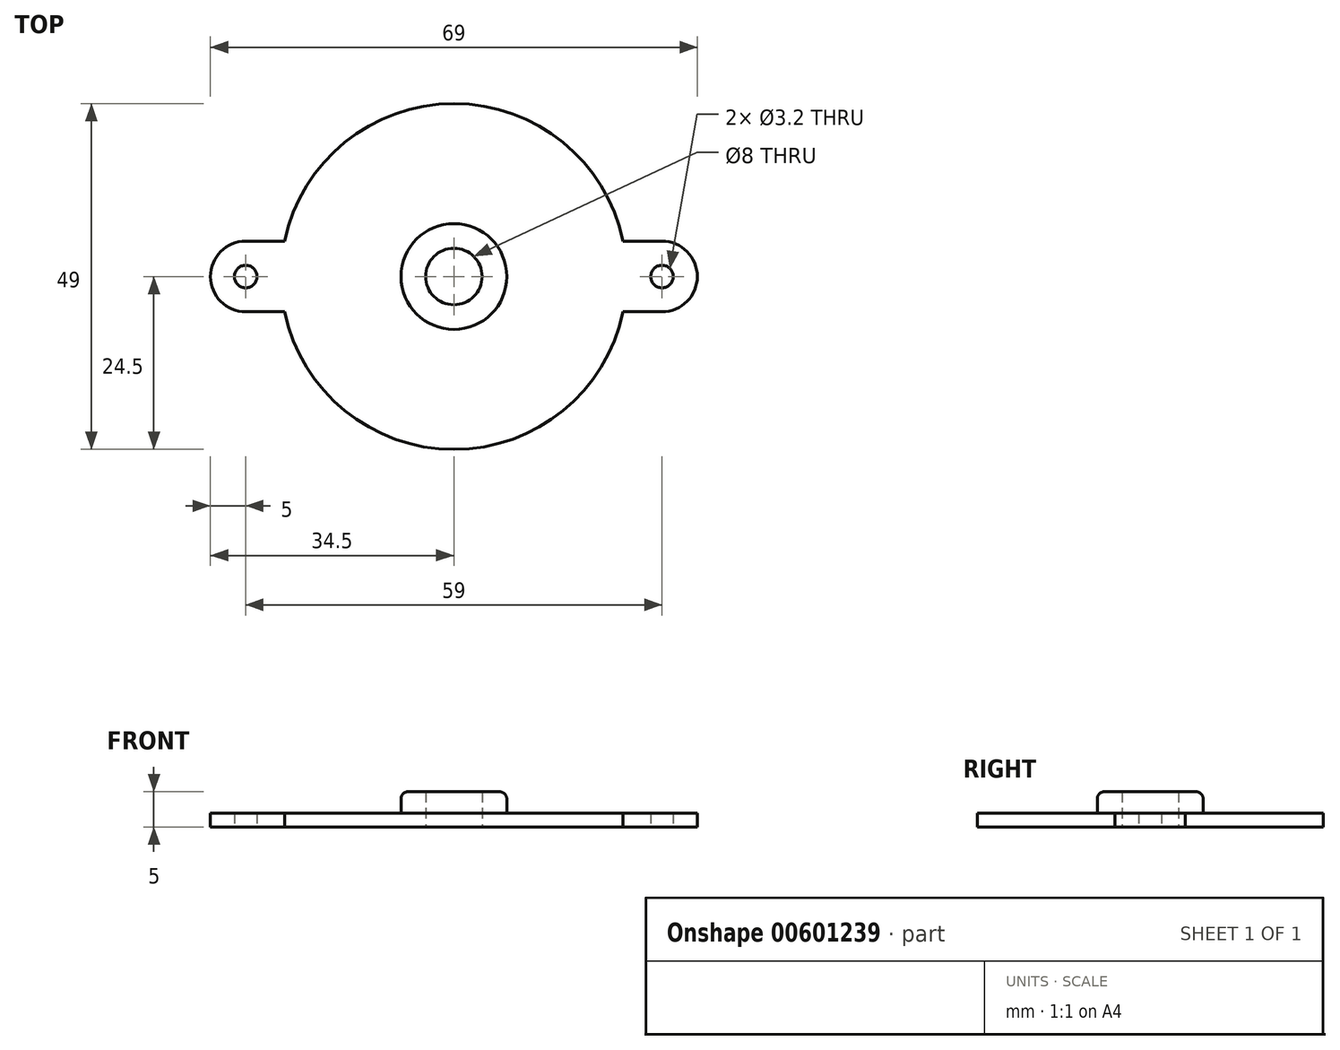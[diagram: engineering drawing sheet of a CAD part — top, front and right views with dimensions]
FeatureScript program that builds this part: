
annotation { "Feature Type Name" : "Feature", "Feature Type Description" : "" }
export const myFeature = defineFeature(function(context is Context, id is Id, definition is map)
    precondition{}
    {
        {
            var Q0;
            Q0=qCreatedBy(makeId("Top.planeOp"),FACE);
            var sketch = newSketch(context, id + "F0", { "sketchPlane" : qUnion([Q0])});
            skCircle(sketch, "E0", {"center": v(-29.5, 0) * mm, "radius": 5 * mm});
            skCircle(sketch, "E1", {"center": v(29.5, 0) * mm, "radius": 5 * mm});
            skCircle(sketch, "E2", {"center": v(-29.5, 0) * mm, "radius": 1.6 * mm});
            skCircle(sketch, "E3", {"center": v(29.5, 0) * mm, "radius": 1.6 * mm});
            skCircle(sketch, "E4", {"center": v(0, 0) * mm, "radius": 24.5 * mm});
            skLineSegment(sketch, "E5", {"start": v(-29.5, 5) * mm, "end": v(-23.98, 5) * mm});
            skLineSegment(sketch, "E6", {"start": v(-29.5, -5) * mm, "end": v(-23.98, -5) * mm});
            skLineSegment(sketch, "E7", {"start": v(23.98, -5) * mm, "end": v(29.5, -5) * mm});
            skLineSegment(sketch, "E8", {"start": v(23.98, 5) * mm, "end": v(29.5, 5) * mm});
            skCircle(sketch, "E9", {"center": v(0, 0) * mm, "radius": 4 * mm});
            skSolve(sketch);
        }
        {
            var Q0;
            Q0=makeQuery(id+"F0.imprint","IMPRINT",FACE,{"disambiguationData":[TD([[makeQuery(id+"F0.imprint","IMPRINT",EDGE,{"derivedFrom":sQuery(id+"F0.wireOp",EDGE,"E2")}),-1.0]])]});
            var Q1;
            {var subQ0=sQuery(id+"F0.wireOp",EDGE,"E5");Q1=makeQuery(id+"F0.imprint","IMPRINT",FACE,{"disambiguationData":[TD([[makeQuery(id+"F0.imprint","IMPRINT",EDGE,{"derivedFrom":subQ0}),-1.0]])]});}
            var Q2;
            {var subQ0=sQuery(id+"F0.wireOp",EDGE,"E6");Q2=makeQuery(id+"F0.imprint","IMPRINT",FACE,{"disambiguationData":[TD([[makeQuery(id+"F0.imprint","IMPRINT",EDGE,{"derivedFrom":subQ0}),1.0]])]});}
            var Q3;
            Q3=makeQuery(id+"F0.imprint","IMPRINT",FACE,{"disambiguationData":[TD([[makeQuery(id+"F0.imprint","IMPRINT",EDGE,{"derivedFrom":sQuery(id+"F0.wireOp",EDGE,"E9")}),-1.0]])]});
            var Q4;
            Q4=makeQuery(id+"F0.imprint","IMPRINT",FACE,{"disambiguationData":[TD([[makeQuery(id+"F0.imprint","IMPRINT",EDGE,{"derivedFrom":sQuery(id+"F0.wireOp",EDGE,"E3")}),-1.0]])]});
            var Q5;
            {var subQ0=sQuery(id+"F0.wireOp",EDGE,"E7");Q5=makeQuery(id+"F0.imprint","IMPRINT",FACE,{"disambiguationData":[TD([[makeQuery(id+"F0.imprint","IMPRINT",EDGE,{"derivedFrom":subQ0}),1.0]])]});}
            var Q6;
            {var subQ0=sQuery(id+"F0.wireOp",EDGE,"E8");Q6=makeQuery(id+"F0.imprint","IMPRINT",FACE,{"disambiguationData":[TD([[makeQuery(id+"F0.imprint","IMPRINT",EDGE,{"derivedFrom":subQ0}),-1.0]])]});}
            extrude(context, id + "F1", {"entities" : qUnion([Q0, Q1, Q2, Q3, Q4, Q5, Q6]), "depth" : 2 * mm, "offsetDistance" : 25 * mm});
        }
        {
            var Q0;
            Q0=makeQuery(id+"F1.opExtrude","CAP_FACE",FACE,{"disambiguationData":[OSD([sQuery(id+"F0.wireOp",EDGE,"E0"),sQuery(id+"F0.wireOp",EDGE,"E1"),sQuery(id+"F0.wireOp",EDGE,"E2"),sQuery(id+"F0.wireOp",EDGE,"E3"),sQuery(id+"F0.wireOp",EDGE,"E4"),sQuery(id+"F0.wireOp",EDGE,"E5"),sQuery(id+"F0.wireOp",EDGE,"E6"),sQuery(id+"F0.wireOp",EDGE,"E7"),sQuery(id+"F0.wireOp",EDGE,"E8"),sQuery(id+"F0.wireOp",EDGE,"E9")])],"isStart":false});
            var sketch = newSketch(context, id + "F2", { "sketchPlane" : qUnion([Q0])});
            skCircle(sketch, "E10", {"center": v(0, 0) * mm, "radius": 4 * mm});
            skCircle(sketch, "E11", {"center": v(0, 0) * mm, "radius": 7.5 * mm});
            skSolve(sketch);
        }
        {
            var Q0;
            Q0=makeQuery(id+"F2.imprint","IMPRINT",FACE,{"disambiguationData":[TD([[makeQuery(id+"F2.imprint","IMPRINT",EDGE,{"derivedFrom":sQuery(id+"F2.wireOp",EDGE,"E10")}),-1.0]])]});
            extrude(context, id + "F3", {"entities" : qUnion([Q0]), "operationType" : NewBodyOperationType.ADD, "depth" : 3 * mm, "offsetDistance" : 25 * mm});
        }
        {
            var Q0;
            Q0=makeQuery(id+"F3.opExtrude","CAP_EDGE",EDGE,{"disambiguationData":[OSD([sQuery(id+"F2.wireOp",EDGE,"E11")])],"isStart":false});
            fillet(context, id + "F4", {"entities" : qUnion([Q0]), "radius" : 1 * mm, "tangentPropagation" : true, "allowEdgeOverflow" : false});
        }
    });
